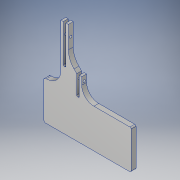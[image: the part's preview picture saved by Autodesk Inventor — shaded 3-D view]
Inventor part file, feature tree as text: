
AUTODESK INVENTOR PART (.ipt)
format: ipt  version: 2019 (Build 230136000, 136)  size: 236,544 bytes
history: native  units: in
note: dims shown in document units (in); Inventor stores cm internally (conversion verified against a paired STEP export)
features: sketch x15, extrude x12, fillet x5
ambient origin geometry x8: Origin, YZ Plane, XZ Plane, XY Plane, X Axis, Y Axis, Z Axis, Center Point
bodies: Solid1 (feature_tree)
feature tree (32):
  extrude  "Extrusion1"  Depth=2.0in
  sketch  "Sketch2"  dims[d3=4.5in d4=0.125in d5=0.0in]
  extrude  "Extrusion2"  Depth=0.125in TaperAngle=0.0deg
  extrude  "Extrusion3"  Depth=0.066in
  extrude  "Extrusion4"  Depth=0.25in
  extrude  "Extrusion5"  Depth=0.125in TaperAngle=0.0deg
  extrude  "Extrusion6"  Depth=3.0in TaperAngle=0.0deg
  sketch  "Sketch6"  dims[d14=3.0in d15=0.0in d16=3.0in d17=0.0in]
  sketch  "Sketch7"  dims[d18=0.75in d19=0.125in]
  sketch  "Sketch8"  dims[d20=2.0in d21=0.0in d22=1.64in]
  sketch  "Sketch9"  dims[d23=0.125in d24=2.0in d25=0.0in]
  extrude  "Extrusion11"  Depth=0.125in
  extrude  "Extrusion12"  Depth=2.0in
  extrude  "Extrusion13"  Depth=2.0in TaperAngle=0.0deg
  extrude  "Extrusion14"  Depth=0.125in
  extrude  "Extrusion15"  Depth=0.125in
  extrude  "Extrusion16"  Depth=0.125in
  fillet  "Fillet1"  Radius=0.25in
  fillet  "Fillet3"  Radius=0.067in
  fillet  "Fillet4"  Radius=0.125in
  fillet  "Fillet5"  Radius=0.25in
  fillet  "Fillet6"  Radius=0.125in
  sketch  "Sketch1"  dims[d1=4.5in d2=2.0in]
  sketch  "Sketch3"  dims[d7=0.066in d8=0.066in]
  sketch  "Sketch4"  dims[d9=0.125in d10=0.25in]
  sketch  "Sketch5"  dims[d11=0.125in d12=0.125in d13=0.0in]
  sketch  "Sketch12"  dims[d30=0.125in d34=0.125in]
  sketch  "Sketch13"  dims[d35=0.132in d36=0.125in]
  sketch  "Sketch14"  dims[d44=0.067in d45=0.125in d46=0.25in d47=0.0in d48=0.067in d49=0.125in d50=0.25in d51=0.0in d52=0.125in]
  sketch  "Sketch15"  dims[d55=0.25in d56=0.0in]
  sketch  "Sketch16"  dims[d57=2.0in d58=0.0in]
  sketch  "Sketch17"  dims[d59=0.25in d60=0.0in d61=0.5in d62=0.0in d63=0.0625in d65=1.0in d67=0.625in d68=0.0625in d69=0.75in]
